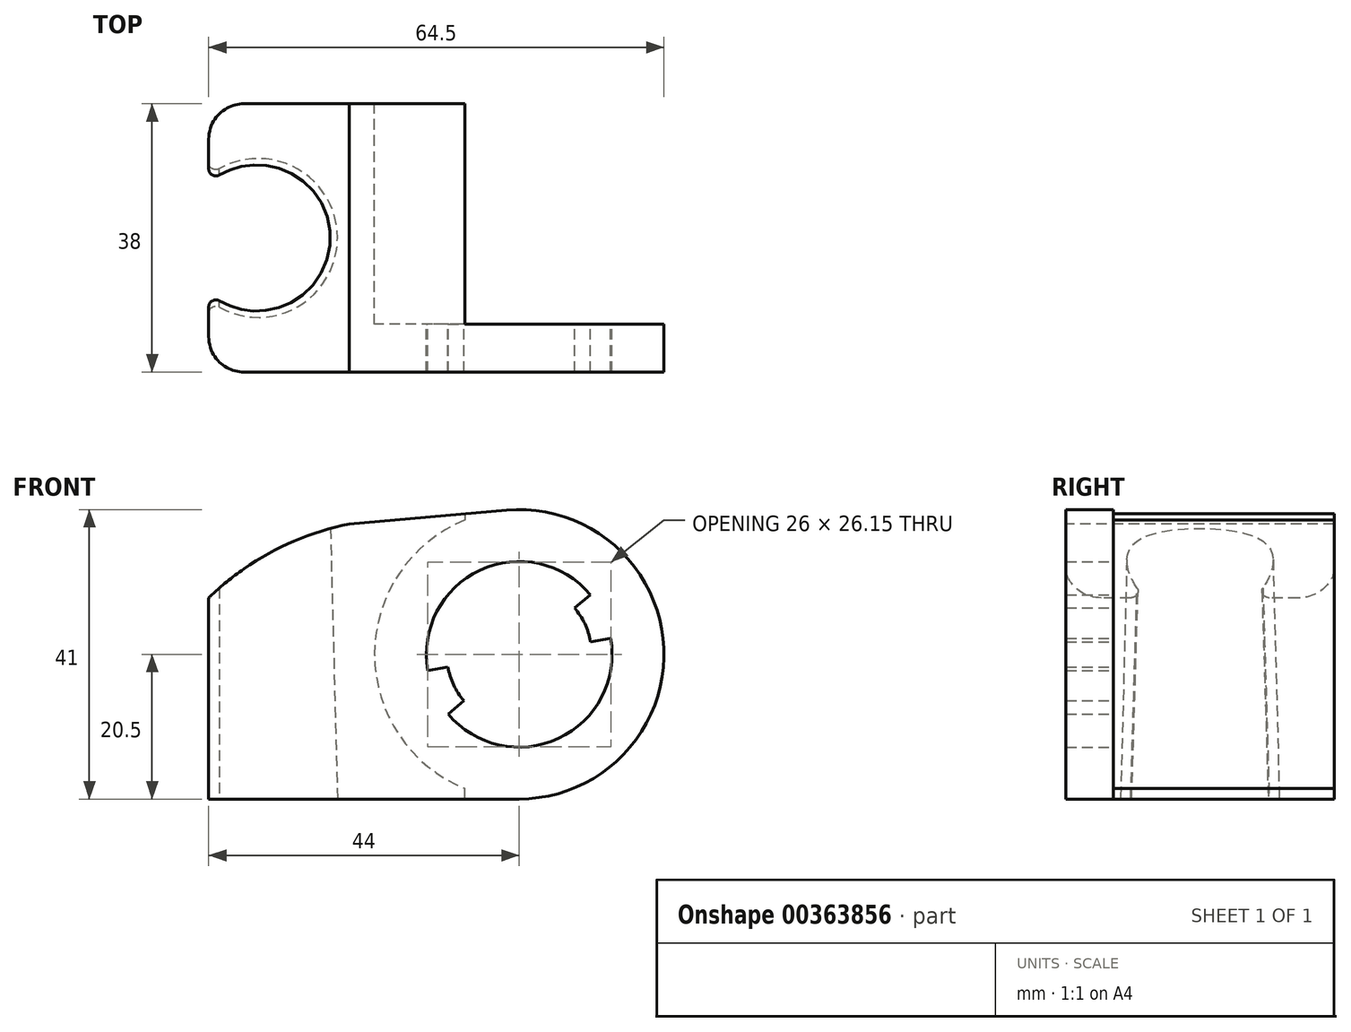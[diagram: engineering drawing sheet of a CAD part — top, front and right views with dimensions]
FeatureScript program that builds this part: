
annotation { "Feature Type Name" : "Feature", "Feature Type Description" : "" }
export const myFeature = defineFeature(function(context is Context, id is Id, definition is map)
    precondition{}
    {
        {
            var Q0;
            Q0=qCreatedBy(makeId("Front.planeOp"),FACE);
            var sketch = newSketch(context, id + "F0", { "sketchPlane" : qUnion([Q0])});
            skCircle(sketch, "E0", {"center": v(0, 0) * mm, "radius": 20.5 * mm});
            skLineSegment(sketch, "E1", {"start": v(0, -20.5) * mm, "end": v(-44, -20.5) * mm});
            skLineSegment(sketch, "E2", {"start": v(-44, -20.5) * mm, "end": v(-44, 16.73) * mm});
            skLineSegment(sketch, "E3", {"start": v(-44, 16.73) * mm, "end": v(0, 20.58) * mm});
            skLineSegment(sketch, "E4", {"start": v(0, 20.58) * mm, "end": v(-44, 20.58) * mm, "construction": true});
            skLineSegment(sketch, "E5", {"start": v(-44, 20.58) * mm, "end": v(-44, 16.73) * mm, "construction": true});
            skCircle(sketch, "E6", {"center": v(0, 0) * mm, "radius": 13.15 * mm});
            skArc(sketch, "E7", {"start": v(-10.1, -1.78) * mm, "mid": v(-9.29, -4.33) * mm, "end": v(-7.85, -6.59) * mm});
            skLineSegment(sketch, "E8", {"start": v(7.85, 6.59) * mm, "end": v(10.08, 8.46) * mm});
            skLineSegment(sketch, "E9", {"start": v(10.1, 1.78) * mm, "end": v(12.95, 2.28) * mm});
            skLineSegment(sketch, "E10", {"start": v(-10.1, -1.78) * mm, "end": v(-12.95, -2.28) * mm});
            skLineSegment(sketch, "E11", {"start": v(-7.85, -6.59) * mm, "end": v(-10.08, -8.46) * mm});
            skArc(sketch, "E12.trimOffspring", {"start": v(10.1, 1.78) * mm, "mid": v(9.29, 4.33) * mm, "end": v(7.85, 6.59) * mm});
            skArc(sketch, "E13", {"start": v(7.85, 6.59) * mm, "mid": v(-4.33, 9.29) * mm, "end": v(-10.1, -1.78) * mm, "construction": true});
            skArc(sketch, "E14", {"start": v(-7.85, -6.59) * mm, "mid": v(4.33, -9.29) * mm, "end": v(10.1, 1.78) * mm, "construction": true});
            skLineSegment(sketch, "E15", {"start": v(0, 0) * mm, "end": v(-7.85, -6.59) * mm, "construction": true});
            skLineSegment(sketch, "E16", {"start": v(0, 0) * mm, "end": v(-10.1, -1.78) * mm, "construction": true});
            skLineSegment(sketch, "E17", {"start": v(0, 0) * mm, "end": v(10.1, 1.78) * mm, "construction": true});
            skLineSegment(sketch, "E18", {"start": v(0, 0) * mm, "end": v(7.85, 6.59) * mm, "construction": true});
            skSolve(sketch);
        }
        {
            var Q0;
            Q0 = qSketchRegion(id + "F0", true);
            var Q1;
            Q1=makeQuery(id+"F0.imprint","IMPRINT",FACE,{"disambiguationData":[TD([[makeQuery(id+"F0.imprint","IMPRINT",EDGE,{"derivedFrom":sQuery(id+"F0.wireOp",EDGE,"E7")}),-1.0]])]});
            var Q2;
            {var subQ0=sQuery(id+"F0.wireOp",EDGE,"E8");Q2=makeQuery(id+"F0.imprint","IMPRINT",FACE,{"disambiguationData":[TD([[makeQuery(id+"F0.imprint","IMPRINT",EDGE,{"derivedFrom":subQ0}),-1.0]])]});}
            extrude(context, id + "F1", {"entities" : qUnion([Q0, Q1, Q2]), "depth" : 38 * mm});
        }
        {
            var Q0;
            Q0=makeQuery(id+"F1.opExtrude","CAP_FACE",FACE,{"disambiguationData":[OSD([sQuery(id+"F0.wireOp",EDGE,"E0"),sQuery(id+"F0.wireOp",EDGE,"E1"),sQuery(id+"F0.wireOp",EDGE,"E2"),sQuery(id+"F0.wireOp",EDGE,"E3"),sQuery(id+"F0.wireOp",EDGE,"E6"),sQuery(id+"F0.wireOp",EDGE,"E7"),sQuery(id+"F0.wireOp",EDGE,"E8"),sQuery(id+"F0.wireOp",EDGE,"E9"),sQuery(id+"F0.wireOp",EDGE,"E10"),sQuery(id+"F0.wireOp",EDGE,"E11"),sQuery(id+"F0.wireOp",EDGE,"E12.trimOffspring")])],"isStart":false});
            var sketch = newSketch(context, id + "F2", { "sketchPlane" : qUnion([Q0])});
            skLineSegment(sketch, "E19", {"start": v(-44, 16.73) * mm, "end": v(-44, 8) * mm});
            skLineSegment(sketch, "E20", {"start": v(-44, 16.73) * mm, "end": v(-24.08, 18.47) * mm});
            skArc(sketch, "E21", {"start": v(-44, 8) * mm, "mid": v(-34.79, 14.67) * mm, "end": v(-24.08, 18.47) * mm});
            skSolve(sketch);
        }
        {
            var Q0;
            Q0=makeQuery(id+"F2.imprint","IMPRINT",FACE,{"disambiguationData":[TD([[makeQuery(id+"F2.imprint","IMPRINT",EDGE,{"derivedFrom":sQuery(id+"F2.wireOp",EDGE,"E19")}),-1.0]])]});
            extrude(context, id + "F3", {"entities" : qUnion([Q0]), "operationType" : NewBodyOperationType.REMOVE, "endBound" : BoundingType.THROUGH_ALL, "oppositeDirection" : true, "depth" : 25 * mm});
        }
        {
            var Q0;
            Q0=makeQuery(id+"F1.opExtrude","CAP_FACE",FACE,{"disambiguationData":[OSD([sQuery(id+"F0.wireOp",EDGE,"E0"),sQuery(id+"F0.wireOp",EDGE,"E1"),sQuery(id+"F0.wireOp",EDGE,"E2"),sQuery(id+"F0.wireOp",EDGE,"E3"),sQuery(id+"F0.wireOp",EDGE,"E6"),sQuery(id+"F0.wireOp",EDGE,"E7"),sQuery(id+"F0.wireOp",EDGE,"E8"),sQuery(id+"F0.wireOp",EDGE,"E9"),sQuery(id+"F0.wireOp",EDGE,"E10"),sQuery(id+"F0.wireOp",EDGE,"E11"),sQuery(id+"F0.wireOp",EDGE,"E12.trimOffspring")])],"isStart":true});
            var sketch = newSketch(context, id + "F4", { "sketchPlane" : qUnion([Q0])});
            skCircle(sketch, "E22", {"center": v(0, 0) * mm, "radius": 20.5 * mm});
            skLineSegment(sketch, "E23", {"start": v(7.7, -20.5) * mm, "end": v(0, -20.5) * mm});
            skLineSegment(sketch, "E24", {"start": v(0, 20.5) * mm, "end": v(7.7, 20.5) * mm});
            skLineSegment(sketch, "E25", {"start": v(7.7, 20.5) * mm, "end": v(7.7, 19) * mm});
            skLineSegment(sketch, "E26", {"start": v(7.7, -20.5) * mm, "end": v(7.7, -19) * mm});
            skSolve(sketch);
        }
        {
            var Q0;
            Q0=makeQuery(id+"F4.imprint","IMPRINT",FACE,{"disambiguationData":[TD([[makeQuery(id+"F4.imprint","IMPRINT",EDGE,{"derivedFrom":makeQuery(id+"F1.opExtrude","CAP_EDGE",EDGE,{"disambiguationData":[OSD([sQuery(id+"F0.wireOp",EDGE,"E7")])],"isStart":true})}),1.0]])]});
            var Q1;
            {var subQ0=sQuery(id+"F4.wireOp",EDGE,"E23");Q1=makeQuery(id+"F4.imprint","IMPRINT",FACE,{"disambiguationData":[TD([[makeQuery(id+"F4.imprint","IMPRINT",EDGE,{"derivedFrom":subQ0}),1.0]])]});}
            var Q2;
            {var subQ3=sQuery(id+"F4.wireOp",EDGE,"E24");Q2=makeQuery(id+"F4.imprint","IMPRINT",FACE,{"disambiguationData":[TD([[makeQuery(id+"F4.imprint","IMPRINT",EDGE,{"derivedFrom":subQ3}),-1.0]])]});}
            var Q3;
            {var subQ0=sQuery(id+"F4.wireOp",EDGE,"E22");var subQ3=sQuery(id+"F4.wireOp",EDGE,"E25");var subQ4=makeQuery(id+"F4.imprint","INTERSECT",VERTEX,{"derivedFrom":[subQ0,subQ3]});Q3=makeQuery(id+"F4.imprint","IMPRINT",FACE,{"disambiguationData":[TD([[makeQuery(id+"F4.imprint","IMPRINT",EDGE,{"disambiguationData":[TD([[subQ4,-1.0]])],"derivedFrom":subQ0}),-1.0]])]});}
            extrude(context, id + "F5", {"entities" : qUnion([Q0, Q1, Q2, Q3]), "operationType" : NewBodyOperationType.REMOVE, "oppositeDirection" : true, "depth" : 31.25 * mm});
        }
        {
            var Q0;
            Q0=makeQuery(id+"F1.opExtrude","SWEPT_FACE",FACE,{"disambiguationData":[OSD([sQuery(id+"F0.wireOp",EDGE,"E1")])]});
            var sketch = newSketch(context, id + "F6", { "sketchPlane" : qUnion([Q0])});
            skLineSegment(sketch, "E27", {"start": v(-7.7, 36.5) * mm, "end": v(-44, 33.25) * mm});
            skLineSegment(sketch, "E28", {"start": v(-44, 33.25) * mm, "end": v(-44, 38) * mm});
            skLineSegment(sketch, "E29", {"start": v(-44, 38) * mm, "end": v(-7.7, 36.5) * mm});
            skLineSegment(sketch, "E30", {"start": v(-7.7, 0) * mm, "end": v(-44, 4.75) * mm});
            skLineSegment(sketch, "E31", {"start": v(-44, 4.75) * mm, "end": v(-44, 0) * mm});
            skLineSegment(sketch, "E32", {"start": v(-44, 0) * mm, "end": v(-7.7, 0) * mm});
            skLineSegment(sketch, "E33", {"start": v(-44, 19) * mm, "end": v(-7.7, 19) * mm, "construction": true});
            skLineSegment(sketch, "E34", {"start": v(-7.7, 0) * mm, "end": v(-7.7, 36.5) * mm, "construction": true});
            skSolve(sketch);
        }
        {
            var Q0;
            Q0=makeQuery(id+"F1.opExtrude","CAP_FACE",FACE,{"disambiguationData":[OSD([sQuery(id+"F0.wireOp",EDGE,"E0"),sQuery(id+"F0.wireOp",EDGE,"E1"),sQuery(id+"F0.wireOp",EDGE,"E2"),sQuery(id+"F0.wireOp",EDGE,"E3"),sQuery(id+"F0.wireOp",EDGE,"E6"),sQuery(id+"F0.wireOp",EDGE,"E7"),sQuery(id+"F0.wireOp",EDGE,"E8"),sQuery(id+"F0.wireOp",EDGE,"E9"),sQuery(id+"F0.wireOp",EDGE,"E10"),sQuery(id+"F0.wireOp",EDGE,"E11"),sQuery(id+"F0.wireOp",EDGE,"E12.trimOffspring")])],"isStart":true});
            var sketch = newSketch(context, id + "F7", { "sketchPlane" : qUnion([Q0])});
            skCircle(sketch, "E35", {"center": v(0, 0) * mm, "radius": 20.5 * mm});
            skSolve(sketch);
        }
        {
            var Q0;
            Q0=makeQuery(id+"F1.opExtrude","SWEPT_FACE",FACE,{"disambiguationData":[OSD([sQuery(id+"F0.wireOp",EDGE,"E1")])]});
            var sketch = newSketch(context, id + "F8", { "sketchPlane" : qUnion([Q0])});
            skLineSegment(sketch, "E36", {"start": v(-44, 19) * mm, "end": v(-7.7, 19) * mm, "construction": true});
            skCircle(sketch, "E37", {"center": v(-37, 19) * mm, "radius": 11.25 * mm});
            skSolve(sketch);
        }
        {
            var Q0;
            Q0 = qSketchRegion(id + "F8", true);
            extrude(context, id + "F9", {"entities" : qUnion([Q0]), "operationType" : NewBodyOperationType.REMOVE, "flatOperationType" : FlatOperationType.REMOVE, "endBound" : BoundingType.THROUGH_ALL, "oppositeDirection" : true, "offsetDistance" : 25 * mm, "depth" : 25 * mm, "hasDraft" : true, "draftAngle" : 1.5 * degree, "draftPullDirection" : true, "domain" : OperationDomain.MODEL});
        }
        {
            var Q0;
            Q0=makeQuery(id+"F1.opExtrude","CAP_EDGE",EDGE,{"disambiguationData":[OSD([sQuery(id+"F0.wireOp",EDGE,"E2")])],"isStart":false});
            var Q1;
            Q1=makeQuery(id+"F1.opExtrude","CAP_EDGE",EDGE,{"disambiguationData":[OSD([sQuery(id+"F0.wireOp",EDGE,"E2")])],"isStart":true});
            fillet(context, id + "F10", {"entities" : qUnion([Q0, Q1]), "radius" : 5 * mm, "tangentPropagation" : true, "allowEdgeOverflow" : false});
        }
        {
            var Q0;
            Q0=makeQuery(id+"F9.boolean.opBoolean","INTERSECT",EDGE,{"disambiguationData":[OD(0.0)],"derivedFrom":[makeQuery(id+"F1.opExtrude","SWEPT_FACE",FACE,{"disambiguationData":[OSD([sQuery(id+"F0.wireOp",EDGE,"E2")])]}),makeQuery(id+"F9.opExtrude","SWEPT_FACE",FACE,{"disambiguationData":[OSD([sQuery(id+"F8.wireOp",EDGE,"E37")])]})]});
            var Q1;
            Q1=makeQuery(id+"F9.boolean.opBoolean","INTERSECT",EDGE,{"disambiguationData":[OD(1.0)],"derivedFrom":[makeQuery(id+"F1.opExtrude","SWEPT_FACE",FACE,{"disambiguationData":[OSD([sQuery(id+"F0.wireOp",EDGE,"E2")])]}),makeQuery(id+"F9.opExtrude","SWEPT_FACE",FACE,{"disambiguationData":[OSD([sQuery(id+"F8.wireOp",EDGE,"E37")])]})]});
            fillet(context, id + "F11", {"entities" : qUnion([Q0, Q1]), "radius" : 1 * mm, "tangentPropagation" : true, "allowEdgeOverflow" : false});
        }
    });
